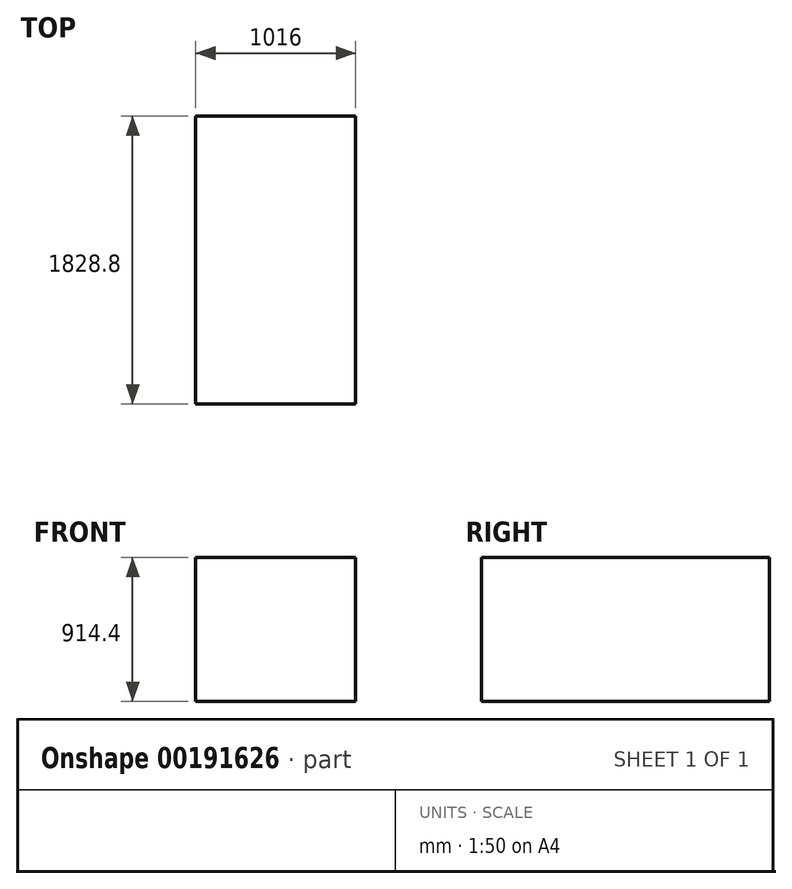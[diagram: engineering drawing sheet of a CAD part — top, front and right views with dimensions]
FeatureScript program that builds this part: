
annotation { "Feature Type Name" : "Feature", "Feature Type Description" : "" }
export const myFeature = defineFeature(function(context is Context, id is Id, definition is map)
    precondition{}
    {
        {
            var Q0;
            Q0=qCreatedBy(makeId("Top.planeOp"),FACE);
            var sketch = newSketch(context, id + "F0", { "sketchPlane" : qUnion([Q0])});
            skLineSegment(sketch, "E0.bottom", {"start": v(0, 0) * mm, "end": v(1016, 0) * mm});
            skLineSegment(sketch, "E0.top", {"start": v(0, -1828.8) * mm, "end": v(1016, -1828.8) * mm});
            skLineSegment(sketch, "E0.left", {"start": v(0, 0) * mm, "end": v(0, -1828.8) * mm});
            skLineSegment(sketch, "E0.right", {"start": v(1016, 0) * mm, "end": v(1016, -1828.8) * mm});
            skSolve(sketch);
        }
        {
            var Q0;
            Q0=makeQuery(id+"F0.imprint","IMPRINT",FACE,{"disambiguationData":[TD([[makeQuery(id+"F0.imprint","IMPRINT",EDGE,{"derivedFrom":sQuery(id+"F0.wireOp",EDGE,"E0.bottom")}),-1.0]])]});
            extrude(context, id + "F1", {"entities" : qUnion([Q0]), "depth" : 914.4 * mm});
        }
    });
